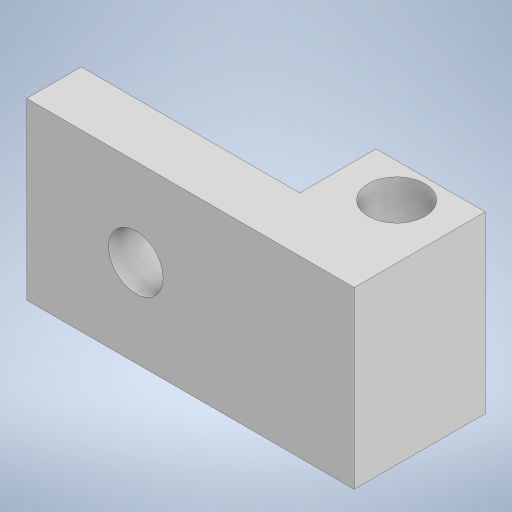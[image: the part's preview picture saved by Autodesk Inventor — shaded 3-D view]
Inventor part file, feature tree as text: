
AUTODESK INVENTOR PART (.ipt)
format: ipt  version: 2023 (Build 270158000, 158)  size: 219,136 bytes
history: native  units: in
note: dims shown in document units (in); Inventor stores cm internally (conversion verified against a paired STEP export)
features: extrude x4, sketch x4
ambient origin geometry x8: Origin, YZ Plane, XZ Plane, XY Plane, X Axis, Y Axis, Z Axis, Center Point
bodies: Solid1 (feature_tree)
feature tree (8):
  extrude  "Extrusion1"  Depth=0.6299in
  extrude  "Extrusion2"  Depth=0.3937in
  extrude  "Extrusion3"  Depth=0.1969in TaperAngle=0.0deg
  extrude  "Extrusion4"  Depth=0.2756in
  sketch  "Sketch1"  dims[d0=0.7874in d1=0.6299in]
  sketch  "Sketch2"  dims[d2=0.315in d3=0.3937in]
  sketch  "Sketch3"  dims[d4=0.1969in d5=0.1969in d6=0.0in]
  sketch  "Sketch4"  dims[d7=0.3937in d8=0.2756in d9=0.2047in d10=0.6299in d11=0.0in d12=0.3543in d13=0.0in d14=0.1969in d15=0.0in d16=0.2047in]
